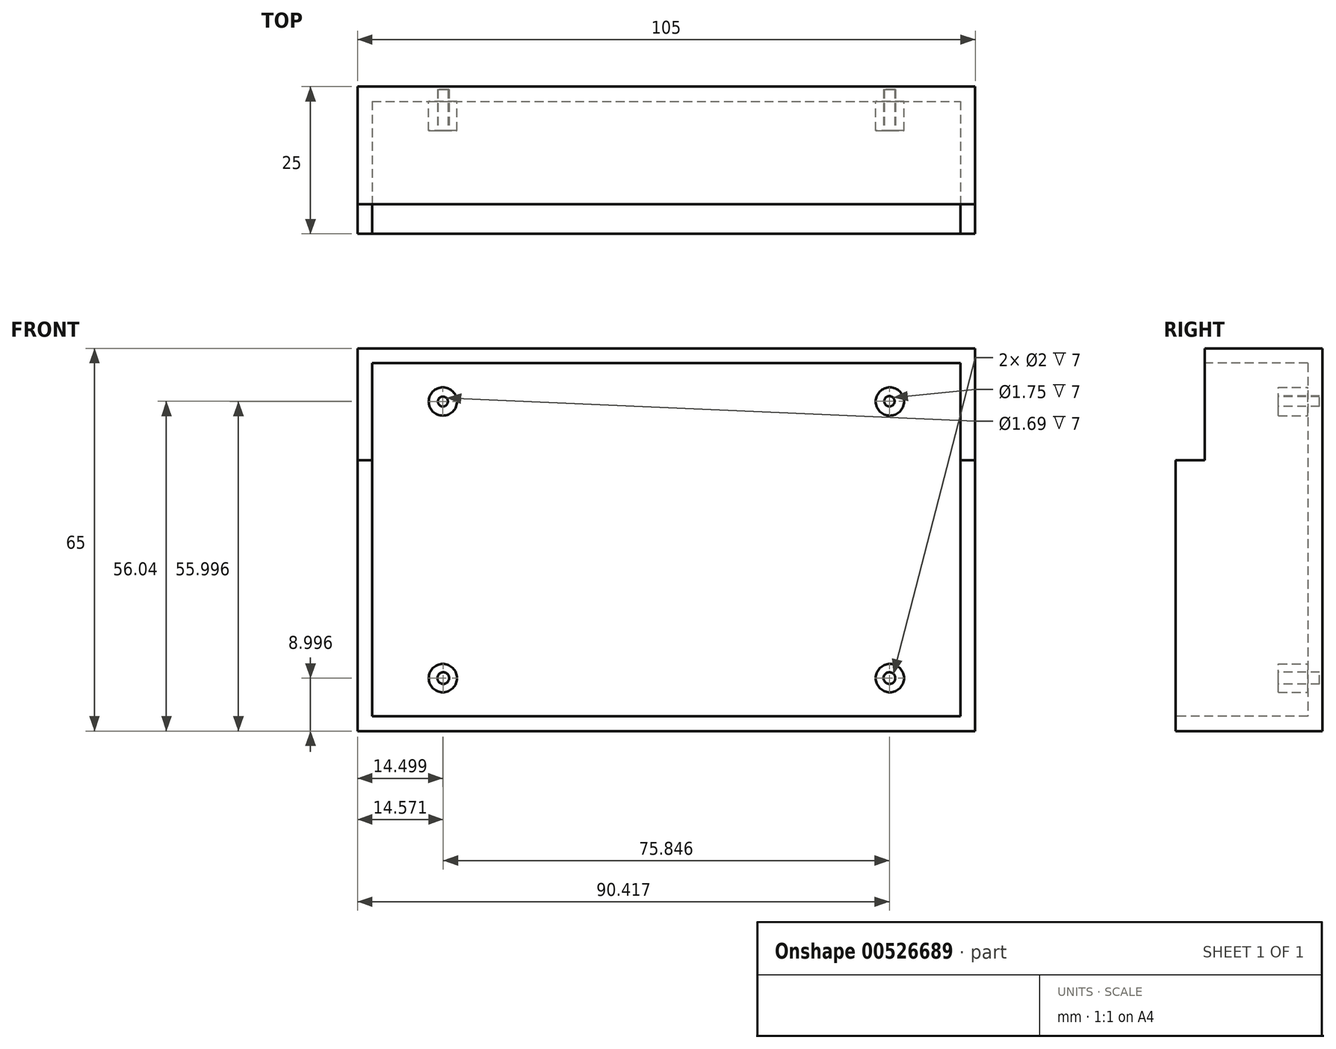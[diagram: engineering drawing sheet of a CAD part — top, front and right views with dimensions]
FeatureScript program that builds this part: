
annotation { "Feature Type Name" : "Feature", "Feature Type Description" : "" }
export const myFeature = defineFeature(function(context is Context, id is Id, definition is map)
    precondition{}
    {
        {
            var Q0;
            Q0=qCreatedBy(makeId("Front.planeOp"),FACE);
            var sketch = newSketch(context, id + "F0", { "sketchPlane" : qUnion([Q0])});
            skLineSegment(sketch, "E0", {"start": v(-41.66, -38.06) * mm, "end": v(63.34, -38.06) * mm});
            skLineSegment(sketch, "E1", {"start": v(63.34, -38.06) * mm, "end": v(63.34, 26.94) * mm});
            skLineSegment(sketch, "E2", {"start": v(63.34, 26.94) * mm, "end": v(-41.66, 26.94) * mm});
            skLineSegment(sketch, "E3", {"start": v(-41.66, 26.94) * mm, "end": v(-41.66, -38.06) * mm});
            skSolve(sketch);
        }
        {
            var Q0;
            Q0=makeQuery(id+"F0.imprint","IMPRINT",FACE,{"disambiguationData":[TD([[makeQuery(id+"F0.imprint","IMPRINT",EDGE,{"derivedFrom":sQuery(id+"F0.wireOp",EDGE,"E0")}),1.0]])]});
            extrude(context, id + "F1", {"entities" : qUnion([Q0]), "depth" : 25 * mm, "offsetDistance" : 25 * mm});
        }
        {
            var Q0;
            Q0=makeQuery(id+"F1.opExtrude","CAP_FACE",FACE,{"disambiguationData":[OSD([sQuery(id+"F0.wireOp",EDGE,"E0"),sQuery(id+"F0.wireOp",EDGE,"E1"),sQuery(id+"F0.wireOp",EDGE,"E2"),sQuery(id+"F0.wireOp",EDGE,"E3")])],"isStart":false});
            var sketch = newSketch(context, id + "F2", { "sketchPlane" : qUnion([Q0])});
            skLineSegment(sketch, "E4", {"start": v(-39.16, 24.44) * mm, "end": v(60.84, 24.44) * mm});
            skLineSegment(sketch, "E5", {"start": v(60.84, 24.44) * mm, "end": v(60.84, -35.56) * mm});
            skLineSegment(sketch, "E6", {"start": v(60.84, -35.56) * mm, "end": v(-39.16, -35.56) * mm});
            skLineSegment(sketch, "E7", {"start": v(-39.16, -35.56) * mm, "end": v(-39.16, 24.44) * mm});
            skLineSegment(sketch, "E8", {"start": v(60.84, -26.72) * mm, "end": v(63.34, -26.72) * mm});
            skLineSegment(sketch, "E9", {"start": v(-41.66, -11.77) * mm, "end": v(-39.16, -11.77) * mm});
            skLineSegment(sketch, "E10", {"start": v(11.93, -35.56) * mm, "end": v(11.93, -38.06) * mm});
            skLineSegment(sketch, "E11", {"start": v(12.48, 26.94) * mm, "end": v(12.48, 24.44) * mm});
            skSolve(sketch);
        }
        {
            var Q0;
            {var subQ4=sQuery(id+"F2.wireOp",EDGE,"E4");var subQ7=sQuery(id+"F2.wireOp",EDGE,"E7");var subQ8=makeQuery(id+"F2.imprint","INTERSECT",VERTEX,{"derivedFrom":[subQ4,subQ7]});Q0=makeQuery(id+"F2.imprint","IMPRINT",FACE,{"disambiguationData":[TD([[makeQuery(id+"F2.imprint","IMPRINT",EDGE,{"disambiguationData":[TD([[subQ8,-1.0]])],"derivedFrom":subQ4}),-1.0]])]});}
            extrude(context, id + "F3", {"entities" : qUnion([Q0]), "operationType" : NewBodyOperationType.REMOVE, "oppositeDirection" : true, "depth" : 22.5 * mm, "offsetDistance" : 25 * mm});
        }
        {
            var Q0;
            Q0=makeQuery(id+"F1.opExtrude","SWEPT_FACE",FACE,{"disambiguationData":[OSD([sQuery(id+"F0.wireOp",EDGE,"E3")])]});
            var sketch = newSketch(context, id + "F4", { "sketchPlane" : qUnion([Q0])});
            skLineSegment(sketch, "E12", {"start": v(25, 7.94) * mm, "end": v(20, 7.94) * mm});
            skLineSegment(sketch, "E13", {"start": v(20, 7.94) * mm, "end": v(20, 26.94) * mm});
            skLineSegment(sketch, "E14", {"start": v(20, 26.94) * mm, "end": v(25, 26.94) * mm});
            skLineSegment(sketch, "E15", {"start": v(25, 26.94) * mm, "end": v(25, 7.94) * mm});
            skSolve(sketch);
        }
        {
            var Q0;
            Q0=makeQuery(id+"F4.imprint","IMPRINT",FACE,{"disambiguationData":[TD([[makeQuery(id+"F4.imprint","IMPRINT",EDGE,{"derivedFrom":sQuery(id+"F4.wireOp",EDGE,"E12")}),-1.0]])]});
            extrude(context, id + "F5", {"entities" : qUnion([Q0]), "operationType" : NewBodyOperationType.REMOVE, "oppositeDirection" : true, "depth" : 2.5 * mm, "offsetDistance" : 25 * mm});
        }
        {
            var Q0;
            Q0=makeQuery(id+"F1.opExtrude","SWEPT_FACE",FACE,{"disambiguationData":[OSD([sQuery(id+"F0.wireOp",EDGE,"E1")])]});
            var sketch = newSketch(context, id + "F6", { "sketchPlane" : qUnion([Q0])});
            skLineSegment(sketch, "E16", {"start": v(-25, 26.94) * mm, "end": v(-25, 7.94) * mm});
            skLineSegment(sketch, "E17", {"start": v(-20, 7.94) * mm, "end": v(-20, 26.94) * mm});
            skLineSegment(sketch, "E18", {"start": v(-20, 26.94) * mm, "end": v(-25, 26.94) * mm});
            skLineSegment(sketch, "E19", {"start": v(-25, 7.94) * mm, "end": v(-20, 7.94) * mm});
            skSolve(sketch);
        }
        {
            var Q0;
            Q0 = qSketchRegion(id + "F6", true);
            extrude(context, id + "F7", {"entities" : qUnion([Q0]), "operationType" : NewBodyOperationType.REMOVE, "oppositeDirection" : true, "depth" : 2.5 * mm, "offsetDistance" : 25 * mm});
        }
        {
            var Q0;
            Q0=makeQuery(id+"F1.opExtrude","SWEPT_FACE",FACE,{"disambiguationData":[OSD([sQuery(id+"F0.wireOp",EDGE,"E2")])]});
            var sketch = newSketch(context, id + "F8", { "sketchPlane" : qUnion([Q0])});
            skLineSegment(sketch, "E20", {"start": v(-39.16, -22.5) * mm, "end": v(-39.16, -25) * mm});
            skLineSegment(sketch, "E21", {"start": v(-39.16, -25) * mm, "end": v(60.84, -25) * mm});
            skLineSegment(sketch, "E22", {"start": v(60.84, -20) * mm, "end": v(-39.16, -20) * mm});
            skSolve(sketch);
        }
        {
            var Q0;
            {var subQ3=sQuery(id+"F8.wireOp",EDGE,"E20");Q0=makeQuery(id+"F8.imprint","IMPRINT",FACE,{"disambiguationData":[TD([[makeQuery(id+"F8.imprint","IMPRINT",EDGE,{"derivedFrom":subQ3}),-1.0]])]});}
            extrude(context, id + "F9", {"entities" : qUnion([Q0]), "operationType" : NewBodyOperationType.REMOVE, "oppositeDirection" : true, "depth" : 2.5 * mm, "offsetDistance" : 25 * mm});
        }
        {
            var Q0;
            Q0=makeQuery(id+"F3.boolean.opBoolean","COPY",FACE,{"derivedFrom":makeQuery(id+"F3.opExtrude","CAP_FACE",FACE,{"disambiguationData":[OSD([sQuery(id+"F2.wireOp",EDGE,"E4"),sQuery(id+"F2.wireOp",EDGE,"E5"),sQuery(id+"F2.wireOp",EDGE,"E6"),sQuery(id+"F2.wireOp",EDGE,"E7")])],"isStart":false})});
            var sketch = newSketch(context, id + "F10", { "sketchPlane" : qUnion([Q0])});
            skCircle(sketch, "E23", {"center": v(-27.16, 17.94) * mm, "radius": 2.4 * mm});
            skCircle(sketch, "E24", {"center": v(48.84, 17.94) * mm, "radius": 2.4 * mm});
            skCircle(sketch, "E25", {"center": v(-27.16, -29.06) * mm, "radius": 2.4 * mm});
            skCircle(sketch, "E26", {"center": v(48.84, -29.06) * mm, "radius": 2.4 * mm});
            skSolve(sketch);
        }
        {
            var Q0;
            Q0=makeQuery(id+"F10.imprint","IMPRINT",FACE,{"disambiguationData":[TD([[makeQuery(id+"F10.imprint","IMPRINT",EDGE,{"derivedFrom":sQuery(id+"F10.wireOp",EDGE,"E24")}),1.0]])]});
            var Q1;
            Q1=makeQuery(id+"F10.imprint","IMPRINT",FACE,{"disambiguationData":[TD([[makeQuery(id+"F10.imprint","IMPRINT",EDGE,{"derivedFrom":sQuery(id+"F10.wireOp",EDGE,"E25")}),1.0]])]});
            var Q2;
            Q2=makeQuery(id+"F10.imprint","IMPRINT",FACE,{"disambiguationData":[TD([[makeQuery(id+"F10.imprint","IMPRINT",EDGE,{"derivedFrom":sQuery(id+"F10.wireOp",EDGE,"E26")}),1.0]])]});
            var Q3;
            Q3=makeQuery(id+"F10.imprint","IMPRINT",FACE,{"disambiguationData":[TD([[makeQuery(id+"F10.imprint","IMPRINT",EDGE,{"derivedFrom":sQuery(id+"F10.wireOp",EDGE,"E23")}),1.0]])]});
            extrude(context, id + "F11", {"entities" : qUnion([Q0, Q1, Q2, Q3]), "operationType" : NewBodyOperationType.ADD, "depth" : 5 * mm, "offsetDistance" : 25 * mm});
        }
        {
            var Q0;
            Q0=makeQuery(id+"F11.opExtrude","CAP_FACE",FACE,{"disambiguationData":[OSD([sQuery(id+"F10.wireOp",EDGE,"E23")])],"isStart":false});
            var sketch = newSketch(context, id + "F12", { "sketchPlane" : qUnion([Q0])});
            skCircle(sketch, "E27", {"center": v(-27.16, 17.94) * mm, "radius": 0.85 * mm});
            skCircle(sketch, "E28", {"center": v(48.76, 17.98) * mm, "radius": 0.87 * mm});
            skCircle(sketch, "E29", {"center": v(48.76, -29.06) * mm, "radius": 1 * mm});
            skCircle(sketch, "E30", {"center": v(-27.09, -29.06) * mm, "radius": 1 * mm});
            skSolve(sketch);
        }
        {
            var Q0;
            Q0=makeQuery(id+"F12.imprint","IMPRINT",FACE,{"disambiguationData":[TD([[makeQuery(id+"F12.imprint","IMPRINT",EDGE,{"derivedFrom":sQuery(id+"F12.wireOp",EDGE,"E28")}),1.0]])]});
            var Q1;
            Q1=makeQuery(id+"F12.imprint","IMPRINT",FACE,{"disambiguationData":[TD([[makeQuery(id+"F12.imprint","IMPRINT",EDGE,{"derivedFrom":sQuery(id+"F12.wireOp",EDGE,"E29")}),1.0]])]});
            var Q2;
            Q2=makeQuery(id+"F12.imprint","IMPRINT",FACE,{"disambiguationData":[TD([[makeQuery(id+"F12.imprint","IMPRINT",EDGE,{"derivedFrom":sQuery(id+"F12.wireOp",EDGE,"E27")}),1.0]])]});
            var Q3;
            Q3=makeQuery(id+"F12.imprint","IMPRINT",FACE,{"disambiguationData":[TD([[makeQuery(id+"F12.imprint","IMPRINT",EDGE,{"derivedFrom":sQuery(id+"F12.wireOp",EDGE,"E30")}),1.0]])]});
            extrude(context, id + "F13", {"entities" : qUnion([Q0, Q1, Q2, Q3]), "operationType" : NewBodyOperationType.REMOVE, "oppositeDirection" : true, "depth" : 7 * mm, "offsetDistance" : 25 * mm});
        }
    });
